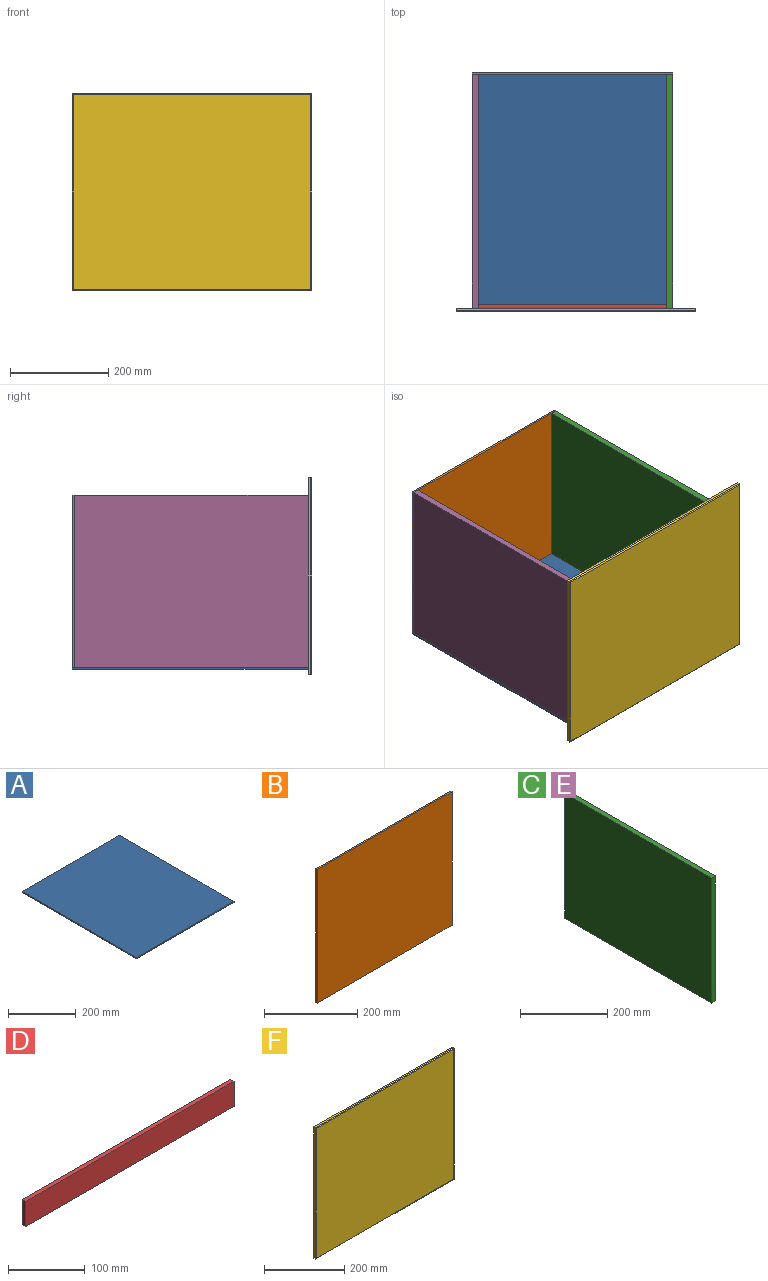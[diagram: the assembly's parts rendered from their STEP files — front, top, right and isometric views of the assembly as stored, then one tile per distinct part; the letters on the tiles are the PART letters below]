
ASSEMBLY  parts=6 mates=5
PART A: 6 faces, bbox 408x480x4 mm
  f0: plane 408x4mm, normal (0,-1,0), area 1632mm2, adj f1,f3,f4,f5
  f1: plane 480x4mm, normal (1,0,0), area 1920mm2, adj f0,f2,f4,f5
  f2: plane 408x4mm, normal (0,1,0), area 1632mm2, adj f1,f3,f4,f5
  f3: plane 480x4mm, normal (-1,0,0), area 1920mm2, adj f0,f2,f4,f5
  f4: plane 480x408mm, normal (0,0,1), area 195840mm2, adj f0,f1,f2,f3
  f5: plane 480x408mm, normal (0,0,-1), area 195840mm2, adj f0,f1,f2,f3
PART B: 6 faces, bbox 408x4x350 mm
  f0: plane 408x4mm, normal (0,0,-1), area 1632mm2, adj f1,f3,f4,f5
  f1: plane 350x4mm, normal (1,0,0), area 1400mm2, adj f0,f2,f4,f5
  f2: plane 408x4mm, normal (0,0,1), area 1632mm2, adj f1,f3,f4,f5
  f3: plane 350x4mm, normal (-1,0,0), area 1400mm2, adj f0,f2,f4,f5
  f4: plane 408x350mm, normal (0,-1,0), area 142800mm2, adj f0,f1,f2,f3
  f5: plane 408x350mm, normal (0,1,0), area 142800mm2, adj f0,f1,f2,f3
PART C: 6 faces, bbox 12x476x350 mm
  f0: plane 476x12mm, normal (0,0,-1), area 5712mm2, adj f1,f3,f4,f5
  f1: plane 350x12mm, normal (0,1,0), area 4200mm2, adj f0,f2,f4,f5
  f2: plane 476x12mm, normal (0,0,1), area 5712mm2, adj f1,f3,f4,f5
  f3: plane 350x12mm, normal (0,-1,0), area 4200mm2, adj f0,f2,f4,f5
  f4: plane 476x350mm, normal (1,0,0), area 166600mm2, adj f0,f1,f2,f3
  f5: plane 476x350mm, normal (-1,0,0), area 166600mm2, adj f0,f1,f2,f3
PART D: 6 faces, bbox 384x7x40 mm
  f0: plane 384x7mm, normal (0,0,-1), area 2688mm2, adj f1,f3,f4,f5
  f1: plane 40x7mm, normal (1,0,0), area 280mm2, adj f0,f2,f4,f5
  f2: plane 384x7mm, normal (0,0,1), area 2688mm2, adj f1,f3,f4,f5
  f3: plane 40x7mm, normal (-1,0,0), area 280mm2, adj f0,f2,f4,f5
  f4: plane 384x40mm, normal (0,-1,0), area 15360mm2, adj f0,f1,f2,f3
  f5: plane 384x40mm, normal (0,1,0), area 15360mm2, adj f0,f1,f2,f3
PART E: same geometry as C
PART F: 10 faces, bbox 488x7x400 mm
  f0: plane 488x5mm, normal (0,0,-1), area 2440mm2, adj f1,f3,f5,f6
  f1: plane 400x5mm, normal (1,0,0), area 2000mm2, adj f0,f2,f5,f7
  f2: plane 488x5mm, normal (0,0,1), area 2440mm2, adj f1,f3,f5,f9
  f3: plane 400x5mm, normal (-1,0,0), area 2000mm2, adj f0,f2,f5,f8
  f4: plane 484x396mm, normal (0,-1,0), area 191664mm2, adj f6,f7,f8,f9
  f5: plane 488x400mm, normal (0,1,0), area 195200mm2, adj f0,f1,f2,f3
  f6: cylinder r=2mm len=488mm, axis (-1,0,0), area 1528.5mm2, adj f0,f4,f7,f8
  f7: cylinder r=2mm len=400mm, axis (0,0,-1), area 1252.1mm2, adj f1,f4,f6,f9
  f8: cylinder r=2mm len=400mm, axis (0,0,1), area 1252.1mm2, adj f3,f4,f6,f9
  f9: cylinder r=2mm len=488mm, axis (1,0,0), area 1528.5mm2, adj f2,f4,f7,f8
PLACE A at identity
PLACE B t=(0,240,179)mm
PLACE C t=(192,-2,179)mm
PLACE D t=(0,-233,259)mm
PLACE E t=(-204,-2,179)mm
PLACE F t=(7,-240,190)mm
MATE fastened A.f4 <-> B.f0  axis (0,0,1) through (-204,240,4)mm
MATE fastened A.f4 <-> E.f0  axis (0,0,1) through (-204,-240,4)mm
MATE fastened C.f0 <-> A.f4  axis (0,0,-1) through (204,-240,4)mm
MATE fastened F.f5 <-> A.f0  axis (0,1,0) through (7,-240,-10)mm
MATE fastened E.f4 <-> D.f3  axis (1,0,0) through (-192,-240,179)mm
